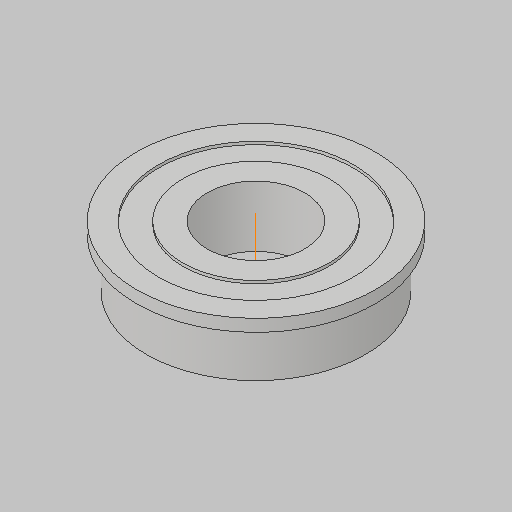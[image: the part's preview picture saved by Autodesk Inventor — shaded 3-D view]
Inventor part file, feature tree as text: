
AUTODESK INVENTOR PART (.ipt)
format: ipt  version: 2023.5 (Build 275446000, 446)  size: 124,416 bytes
history: native  units: in
note: dims shown in document units (in); Inventor stores cm internally (conversion verified against a paired STEP export)
features: revolve x1
ambient origin geometry x8: Origin, YZ Plane, XZ Plane, XY Plane, X Axis, Y Axis, Z Axis, Center Point
bodies: Solid1 (feature_tree)
feature tree (1):
  revolve  "Revolve1"  [1 undecoded]
note: 1 required parameter value undecoded (feature->parameter linkage not recoverable at this tier; creation-order binding heuristic only, values carry confidence <= 0.55)
